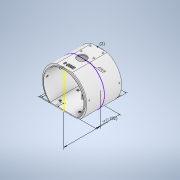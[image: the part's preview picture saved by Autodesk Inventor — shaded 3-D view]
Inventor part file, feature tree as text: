
AUTODESK INVENTOR PART (.ipt)
format: ipt  version: 2020 (Build 240168000, 168)  size: 623,104 bytes
history: native  units: mm
features: sketch x27, other x16, extrude x13, hole x9, plane x1
ambient origin geometry x8: Origin, YZ Plane, XZ Plane, XY Plane, X Axis, Y Axis, Z Axis, Center Point
bodies: Solid1 (feature_tree)
feature tree (66):
  other  "Annotations"
  sketch  "Sketch1"  dims[d8=82.0mm d9=18.0mm d10=0.0mm d11=0.0mm d12=78.0mm d13=0.0mm]
  sketch  "Sketch2"  dims[d19=59.393877mm d64=2.0mm]
  extrude  "Extrusion1"  Depth=78.0mm TaperAngle=0.0deg
  extrude  "Extrusion2"  Depth=2.0mm
  sketch  "Sketch25"  dims[d65=2.0mm d66=82.0mm]
  sketch  "Sketch26"  dims[d67=35.0mm d69=20.0mm]
  plane  "Work Plane8"
  extrude  "Extrusion8"  Depth=2.0mm
  extrude  "Extrusion9"  Depth=20.0mm
  sketch  "Sketch43"  dims[d174=50.0mm d178=70.0mm]
  sketch  "Sketch44"  dims[d182=1.403953mm d185=1.0mm]
  extrude  "Extrusion13"  Depth=0.5mm TaperAngle=0.0deg
  extrude  "Extrusion14"  Depth=50.0mm
  extrude  "Extrusion15"  Depth=70.0mm
  hole  "Hole8"  [1 undecoded]
  hole  "Hole9"  [1 undecoded]
  extrude  "Extrusion16"  Depth=6.0mm
  extrude  "Extrusion18"  Depth=3.0mm
  hole  "Hole10"  [1 undecoded]
  hole  "Hole11"  [1 undecoded]
  hole  "Hole12"  [1 undecoded]
  extrude  "Extrusion19"  Depth=14.525mm
  extrude  "Extrusion20"  Depth=2.3mm
  hole  "Hole13"  [1 undecoded]
  extrude  "Extrusion21"  Depth=20.0mm
  sketch  "Sketch63"  dims[d294=23.5mm d295=1.0mm]
  extrude  "Extrusion22"  Depth=2.0mm
  hole  "Hole14"  [1 undecoded]
  hole  "Hole15"  [1 undecoded]
  hole  "Hole16"  [1 undecoded]
  sketch  "Sketch27"  dims[d70=9.25mm d71=0.0mm d77=0.5mm d78=0.0mm]
  sketch  "Sketch29"  dims[d171=60.0mm d173=50.0mm]
  sketch  "Sketch45"  dims[d186=69.0mm d187=0.0mm d188=11.0mm d189=0.0mm]
  sketch  "Sketch46"  dims[d192=25.04mm d194=6.0mm]
  sketch  "Sketch47"  dims[d195=7.3mm d196=3.0mm]
  sketch  "Sketch50"  dims[d197=3.0mm d198=3.0mm d199=0.0mm]
  sketch  "Sketch51"  dims[d200=3.0mm d201=6.0mm d202=4.0mm d203=2.0mm d204=90.0deg d205=10.5mm d206=20.594885mm]
  sketch  "Sketch53"  dims[d207=3.0mm d208=6.0mm d209=4.0mm d210=2.0mm d211=90.0deg d212=10.5mm d213=20.594885mm d219=5.0mm d220=0.0mm]
  sketch  "Sketch54"  dims[d223=6.0mm d224=0.0mm]
  sketch  "Sketch55"  dims[d232=15.0mm d233=6.0mm d234=4.0mm d235=2.0mm d236=90.0deg d237=10.5mm d238=20.594885mm d262=14.525mm]
  sketch  "Sketch56"  dims[d263=15.0mm d264=14.525mm]
  sketch  "Sketch57"  dims[d265=15.0mm d266=2.3mm]
  sketch  "Sketch58"  dims[d268=7.5mm d269=2.3mm d270=37.5mm]
  sketch  "Sketch60"  dims[d271=2.3mm d272=7.5mm]
  sketch  "Sketch61"  dims[d273=2.3mm d277=3.25mm d278=6.0mm d279=5.0mm d280=0.7mm d281=90.0deg d282=15.664mm d283=0.0mm d291=20.0mm]
  sketch  "Sketch62"  dims[d292=2.0mm d293=2.0mm]
  sketch  "Sketch64"  dims[d296=1.5mm d297=1.5mm]
  sketch  "Sketch65"  dims[d298=1.0mm d299=1.5mm]
  sketch  "Sketch66"  dims[d300=1.0mm]
  sketch  "Sketch67"  dims[d301=1.5mm d302=1.5mm d303=1.0mm d304=3.0mm d305=6.0mm d306=5.0mm d307=0.7mm d308=90.0deg d309=10.5mm d310=20.594885mm d311=14.35mm d333=18.92mm d336=3.15mm d337=8.0mm d338=8.0mm d339=20.0mm d340=0.0mm d341=1.0mm d342=0.0mm d343=2.2mm d344=2.4mm d345=6.0mm d346=4.6mm d347=1.5mm d348=90.0deg d349=24.0mm d350=20.594885mm d360=8.25mm d361=0.0mm d362=8.25mm d363=0.0mm d364=38.4mm d365=6.8mm d366=2.4mm d367=6.0mm d368=4.0mm d369=45.5mm d370=90.0deg d371=69.0mm d372=20.594885mm d373=8.0mm d374=2.5mm d375=6.0mm d376=4.0mm d377=45.5mm d378=90.0deg d379=69.0mm d380=20.594885mm d381=38.4mm d382=6.8mm d383=8.0mm d384=2.5mm d385=6.0mm d386=4.0mm d387=45.75mm d388=90.0deg d389=69.0mm d390=20.594885mm d239=6.080937mm d240=3.441722mm d241=70.0mm d245=2.911617mm d246=9.26364mm d247=20.000012mm d248=3.423786mm d249=8.043699mm d250=91.000003mm d251=2.418403mm d252=7.765244mm d253=14.000018mm d259=1.931685mm d260=6.842692mm d261=3.0mm d285=2.0mm d288=29.760345mm d289=20.0mm d312=4.654013mm d313=4.490862mm d314=71.0mm d316=0.867368mm d317=3.010281mm d321=0.0mm d322=10.0mm d323=69.0mm d326=0.72259mm d327=54.15mm d328=7.921859mm d329=8.058211mm d330=6.368735mm d331=8.781376mm d332=14.35mm d351=5.631667mm d352=6.367341mm d353=19.15mm d354=2.493538mm d355=2.700238mm d356=3.15mm d30=0.5mm d31=0.872665mm d32=0.5mm d33=0.872665mm d79=0.5mm d80=0.872665mm d93=1.0mm d94=1.0mm d95=1.0mm d96=0.15mm d97=5.0mm d98=0.375mm d99=14.3117mm d100=0.75mm d101=20.594885mm d102=0.0625mm d103=0.75mm d104=0.375mm d159=0.5mm d160=0.872665mm d161=0.5mm d162=0.872665mm d172=0.872665mm d179=0.5mm d180=0.872665mm d181=0.5mm d184=0.5mm d221=0.5mm d222=0.872665mm d254=0.5mm d255=0.872665mm d256=0.5mm d257=0.872665mm]
  other  "Linear Dimension 6"
  other  "Linear Dimension 7"
  other  "Linear Dimension 8"
  other  "Linear Dimension 9"
  other  "Linear Dimension 12"
  other  "Linear Dimension 14"
  other  "Diameter Dimension 2"
  other  "Linear Dimension 15"
  other  "Linear Dimension 16"
  other  "Linear Dimension 17"
  other  "Linear Dimension 19"
  other  "Linear Dimension 20"
  other  "Linear Dimension 21"
  other  "Linear Dimension 22"
  other  "Linear Dimension 23"
note: 9 required parameter values undecoded (feature->parameter linkage not recoverable at this tier; creation-order binding heuristic only, values carry confidence <= 0.55)
